# Revit family: RF-3
name_source: partatom
category: Air Terminals
revit_build: Autodesk Revit 2018 (Build: 20170223_1515(x64)
units: mm (PartAtom-declared; Revit-internal decimal feet)

## family parameters
Always vertical = Yes
Cut with Voids When Loaded = No
OmniClass Number = 23.75.00.00
OmniClass Title = Climate Control (HVAC)
Part Type = Normal
Room Calculation Point = No
Round Connector Dimension = Use Diameter
Shared = No
Work Plane-Based = No

## types (9) — shared parameters
Mthick = 0' - 0 1/32"

## per-type parameters (varying)
| type | Adim | Description | Ldim | Manufacturer | Mflange | Model | Mounting | URL | Xdim | Ydim |
| SIZE 5 | 0' - 4 7/8" |  | 1' - 8 5/16" |  | 0' - 3" |  | 0' - 2 15/32" |  | 0' - 9" | 0' - 10 7/8" |
| SIZE 6 | 0' - 5 7/8" | Retrofit, Single Duct W/Velocity Wing Sensor | 1' - 8 5/16" | ANEMOSTAT PRODUCTS | 0' - 2 1/2" | RF-3 | 0' - 2 31/32" | www.anemostat-hvac.com | 0' - 9" | 0' - 10 7/8" |
| SIZE 7 | 0' - 6 7/8" | Retrofit, Single Duct W/Velocity Wing Sensor | 1' - 8 5/16" | ANEMOSTAT PRODUCTS | 0' - 2" | RF-3 | 0' - 3 15/32" | www.anemostat-hvac.com | 0' - 9" | 0' - 10 7/8" |
| SIZE 8 | 0' - 7 7/8" | Retrofit, Single Duct W/Velocity Wing Sensor | 1' - 8 5/16" | ANEMOSTAT PRODUCTS | 0' - 1 1/2" | RF-3 | 0' - 3 31/32" | www.anemostat-hvac.com | 0' - 9" | 0' - 10 7/8" |
| SIZE 9 | 0' - 8 7/8" | Retrofit, Single Duct W/Velocity Wing Sensor | 1' - 8 5/16" | ANEMOSTAT PRODUCTS | 0' - 1 5/8" | RF-3 | 0' - 4 15/32" | www.anemostat-hvac.com | 0' - 9" | 1' - 0 1/8" |
| SIZE 10 | 0' - 9 7/8" | Retrofit, Single Duct W/Velocity Wing Sensor | 1' - 8 5/16" | ANEMOSTAT PRODUCTS | 0' - 1 1/8" | RF-3 | 0' - 4 31/32" | www.anemostat-hvac.com | 0' - 9" | 1' - 0 1/8" |
| SIZE 12 | 0' - 11 7/8" | Retrofit, Single Duct W/Velocity Wing Sensor | 1' - 11 29/32" | ANEMOSTAT PRODUCTS | 0' - 0 3/32" | RF-3 | 0' - 5 31/32" | www.anemostat-hvac.com | 0' - 10" | 1' - 0 1/16" |
| SIZE 14 | 1' - 1 7/8" | Retrofit, Single Duct W/Velocity Wing Sensor | 1' - 11 29/32" | ANEMOSTAT PRODUCTS | 0' - 0 3/32" | RF-3 | 0' - 6 31/32" | www.anemostat-hvac.com | 0' - 10" | 1' - 2 1/16" |
| SIZE 16 | 1' - 3 7/8" | Retrofit, Single Duct W/Velocity Wing Sensor | 1' - 11 29/32" | ANEMOSTAT PRODUCTS | 0' - 0 3/32" | RF-3 | 0' - 7 31/32" | www.anemostat-hvac.com | 0' - 10" | 1' - 4 1/16" |

## geometry (parser evidence)
native form markers: Sweep x3
no freeform markers — native parametric forms only
